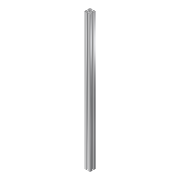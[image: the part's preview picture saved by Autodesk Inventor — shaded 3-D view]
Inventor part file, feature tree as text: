
AUTODESK INVENTOR PART (.ipt)
format: ipt  version: 2019 (Build 230136000, 136)  size: 318,464 bytes
history: native  units: mm
features: other x1, extrude x1, fillet x1, sketch x1
ambient origin geometry x8: Origin, YZ Plane, XZ Plane, XY Plane, X Axis, Y Axis, Z Axis, Center Point
bodies: Body1 (feature_tree)
feature tree (4):
  other  "솔리드1"
  extrude  "돌출1"  Depth=30.0mm
  fillet  "모깎기1"  Radius=30.0mm
  sketch  "스케치1"
